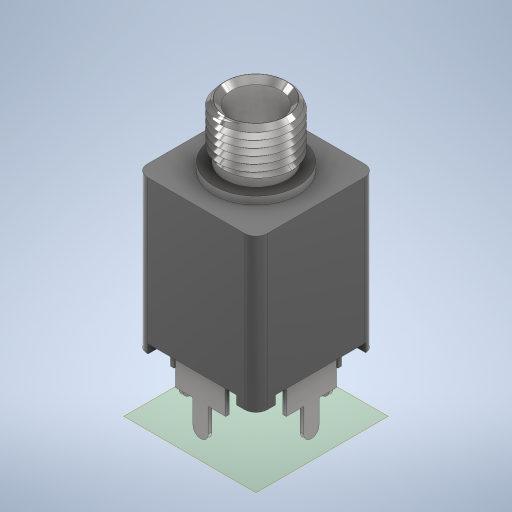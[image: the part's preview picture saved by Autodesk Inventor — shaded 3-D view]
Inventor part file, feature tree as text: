
AUTODESK INVENTOR PART (.ipt)
format: ipt  version: 2023 (Build 270158000, 158)  size: 596,480 bytes
history: native  units: mm
features: projected_geometry x11, sketch x9, extrude x7, fillet x2, plane x2, helix x2, chamfer x1, revolve x1
ambient origin geometry x8: Origin, YZ Plane, XZ Plane, XY Plane, X Axis, Y Axis, Z Axis, Center Point
bodies: Solid1 (feature_tree)
feature tree (35):
  extrude  "Extrusion1"  Depth=15.7mm
  extrude  "Extrusion2"  Depth=11.0mm
  fillet  "Fillet1"  Radius=18.8mm
  extrude  "Extrusion3"  Depth=1.0mm
  extrude  "Extrusion4"  Depth=1.6mm
  extrude  "Extrusion5"  Depth=2.7mm
  chamfer  "Chamfer1"  Distance=2.54mm
  plane  "Work Plane3"
  revolve  "Revolution1"  [1 undecoded]
  sketch  "Sketch7"  dims[d13=2.54mm]
  helix  "Coil1"  [1 undecoded]
  helix  "Coil2"  [1 undecoded]
  extrude  "Extrusion6"  Depth=1.0mm
  extrude  "Extrusion7"  Depth=1.0mm TaperAngle=0.0deg
  fillet  "Fillet3"  Radius=9.34mm
  plane  "Work Plane5"
  sketch  "Sketch1"  dims[d0=15.7mm d1=15.7mm]
  sketch  "Sketch2"  dims[d2=135.0deg d3=11.0mm d4=18.8mm d5=0.0mm]
  projected_geometry  "Projected Loop1"
  sketch  "Sketch3"  dims[d6=4.5mm d7=1.0mm]
  sketch  "Sketch4"  dims[d8=3.7mm d9=1.6mm]
  projected_geometry  "Projected Loop2"
  sketch  "Sketch5"  dims[d10=2.7mm d11=1.71mm]
  projected_geometry  "Projected Loop3"
  sketch  "Sketch6"  dims[d12=2.54mm]
  projected_geometry  "Projected Loop4"
  projected_geometry  "Projected Loop5"
  sketch  "Sketch8"  dims[d14=1.35mm]
  projected_geometry  "Projected Loop6"
  sketch  "Sketch9"  dims[d15=1.35mm d16=2.54mm d17=1.35mm d18=1.14mm d19=0.0mm d20=1.5mm d21=11.0mm d22=1.0mm d23=0.0mm d24=9.34mm d25=7.14mm d26=0.0mm d27=6.46mm d28=17.18mm d29=0.0mm d30=0.7mm d31=2.0mm d32=45.0deg d37=8.16mm d38=1.35mm d39=90.0deg d40=0.9mm d41=0.9mm d42=10.0mm d43=60.0mm d44=0.0mm d45=90.0deg d46=90.0deg d47=0.0mm d48=0.0mm d49=0.9mm d50=10.0mm d51=10.0mm d52=0.0mm d53=90.0deg d54=90.0deg d55=0.0mm d56=0.0mm d57=0.46mm d63=0.46mm d64=0.46mm d65=0.46mm d66=0.46mm d67=6.56mm d68=6.56mm d69=4.27mm d70=4.27mm d71=4.27mm d76=4.37mm d77=0.0mm d78=2.0mm d79=2.0mm d80=2.0mm d81=2.0mm d83=8.51mm d84=0.0mm d86=6.4mm d87=6.4mm d88=6.4mm d89=6.4mm d90=2.4mm d91=4.67mm d92=2.0mm d100=1.0mm d101=9.0mm d104=2.4mm d105=0.6mm d106=0.6mm]
  projected_geometry  "Projected Loop7"
  projected_geometry  "Projected Loop8"
  projected_geometry  "Projected Loop9"
  projected_geometry  "Projected Loop10"
  projected_geometry  "Projected Loop11"
note: 3 required parameter values undecoded (feature->parameter linkage not recoverable at this tier; creation-order binding heuristic only, values carry confidence <= 0.55)